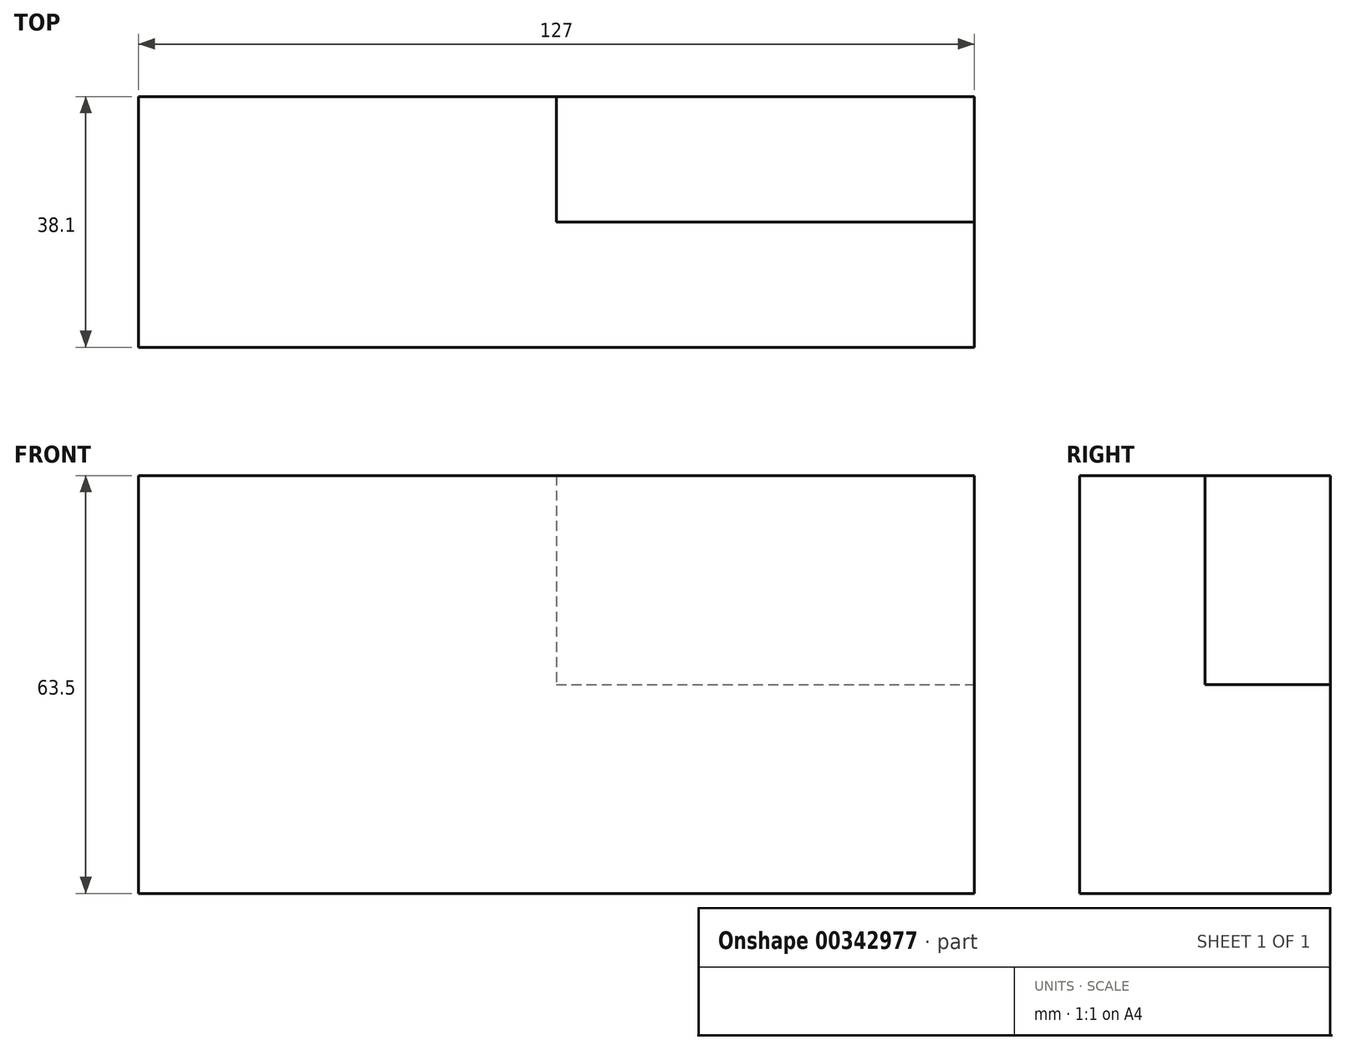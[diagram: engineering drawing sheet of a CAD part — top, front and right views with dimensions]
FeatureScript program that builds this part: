
annotation { "Feature Type Name" : "Feature", "Feature Type Description" : "" }
export const myFeature = defineFeature(function(context is Context, id is Id, definition is map)
    precondition{}
    {
        {
            var Q0;
            Q0=qCreatedBy(makeId("Front.planeOp"),FACE);
            var sketch = newSketch(context, id + "F0", { "sketchPlane" : qUnion([Q0])});
            skLineSegment(sketch, "E0", {"start": v(-68.6, -31.75) * mm, "end": v(58.4, -31.75) * mm});
            skLineSegment(sketch, "E1", {"start": v(-68.6, -31.75) * mm, "end": v(-68.6, 31.75) * mm});
            skLineSegment(sketch, "E2", {"start": v(-5.1, 0) * mm, "end": v(58.4, 0) * mm});
            skLineSegment(sketch, "E3", {"start": v(-5.1, 31.75) * mm, "end": v(-5.1, 0) * mm});
            skLineSegment(sketch, "E4", {"start": v(-68.6, 31.75) * mm, "end": v(58.4, 31.75) * mm});
            skLineSegment(sketch, "E5", {"start": v(58.4, 31.75) * mm, "end": v(58.4, -31.75) * mm});
            skSolve(sketch);
        }
        {
            var Q0;
            {var subQ0=sQuery(id+"F0.wireOp",EDGE,"E2");Q0=makeQuery(id+"F0.imprint","IMPRINT",FACE,{"disambiguationData":[TD([[makeQuery(id+"F0.imprint","IMPRINT",EDGE,{"derivedFrom":subQ0}),1.0]])]});}
            var Q1;
            {var subQ3=sQuery(id+"F0.wireOp",EDGE,"E0");Q1=makeQuery(id+"F0.imprint","IMPRINT",FACE,{"disambiguationData":[TD([[makeQuery(id+"F0.imprint","IMPRINT",EDGE,{"derivedFrom":subQ3}),1.0]])]});}
            extrude(context, id + "F1", {"entities" : qUnion([Q0, Q1]), "depth" : 38.1 * mm});
        }
        {
            var Q0;
            {var subQ0=sQuery(id+"F0.wireOp",EDGE,"E2");Q0=makeQuery(id+"F0.imprint","IMPRINT",FACE,{"disambiguationData":[TD([[makeQuery(id+"F0.imprint","IMPRINT",EDGE,{"derivedFrom":subQ0}),1.0]])]});}
            extrude(context, id + "F2", {"entities" : qUnion([Q0]), "operationType" : NewBodyOperationType.REMOVE, "oppositeDirection" : true, "depth" : 0 * mm, "hasSecondDirection" : true, "secondDirectionOppositeDirection" : false, "secondDirectionDepth" : 19.05 * mm});
        }
    });
